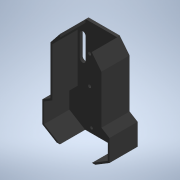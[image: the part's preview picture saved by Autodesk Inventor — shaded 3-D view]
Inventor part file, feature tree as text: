
AUTODESK INVENTOR PART (.ipt)
format: ipt  version: 2021 (Build 250183000, 183)  size: 265,728 bytes
history: native  units: mm
features: extrude x5, sketch x3, projected_geometry x1
ambient origin geometry x8: Origin, YZ Plane, XZ Plane, XY Plane, X Axis, Y Axis, Z Axis, Center Point
bodies: Solid1 (feature_tree)
feature tree (9):
  extrude  "Extrusion1"  Depth=3.0mm TaperAngle=0.0deg
  sketch  "Sketch2"  dims[d9=29.0mm d10=10.0mm]
  extrude  "Extrusion2"  Depth=10.0mm
  extrude  "Extrusion3"  Depth=16.5mm
  sketch  "Sketch3"  dims[d11=10.0mm d12=16.5mm d13=16.5mm d14=40.0mm d15=2.0mm d16=2.0mm d17=2.0mm d18=2.0mm d19=2.0mm d20=2.0mm d21=29.0mm d22=0.0mm d26=0.2mm d27=0.2mm d28=0.2mm d29=0.2mm d30=0.2mm d31=0.2mm d32=20.0mm d33=0.0mm d34=8.2mm d35=8.2mm d36=2.0mm d37=2.0mm d39=2.0mm d41=20.0mm d42=0.0mm d43=20.0mm d44=0.0mm d46=50.0mm d47=0.2mm d48=0.2mm d49=10.0mm d50=6.0mm d52=22.0mm d53=12.0mm d59=2.8mm d60=35.0mm d61=10.0mm d62=10.0mm d70=59.6mm d72=29.6mm d73=3.2mm d74=24.0mm d75=12.0mm d77=0.85mm]
  extrude  "Extrusion4"  Depth=16.5mm
  extrude  "Extrusion5"  Depth=10.0mm
  sketch  "Sketch1"  dims[d0=32.0mm d2=3.0mm d3=0.0mm]
  projected_geometry  "Projected Loop1"
